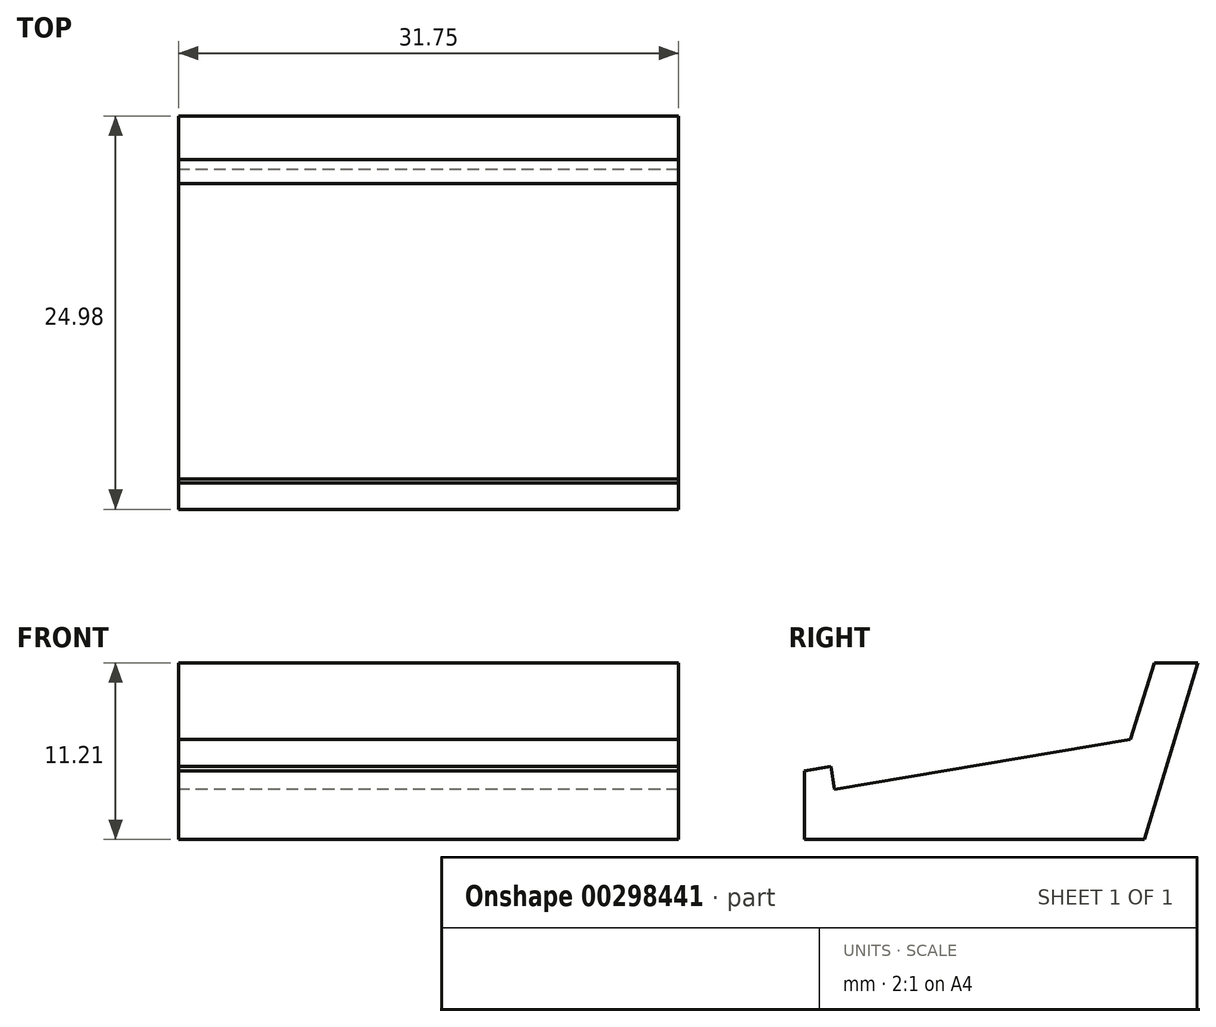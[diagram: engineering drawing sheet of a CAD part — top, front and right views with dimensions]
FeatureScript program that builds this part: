
annotation { "Feature Type Name" : "Feature", "Feature Type Description" : "" }
export const myFeature = defineFeature(function(context is Context, id is Id, definition is map)
    precondition{}
    {
        {
            var Q0;
            Q0=qCreatedBy(makeId("Right.planeOp"),FACE);
            var sketch = newSketch(context, id + "F0", { "sketchPlane" : qUnion([Q0])});
            skLineSegment(sketch, "E0", {"start": v(0, 0) * mm, "end": v(21.59, 0) * mm});
            skLineSegment(sketch, "E1", {"start": v(21.6, 0) * mm, "end": v(24.98, 11.21) * mm});
            skLineSegment(sketch, "E2", {"start": v(24.98, 11.21) * mm, "end": v(22.22, 11.21) * mm});
            skLineSegment(sketch, "E3", {"start": v(22.22, 11.21) * mm, "end": v(20.7, 6.35) * mm});
            skLineSegment(sketch, "E4", {"start": v(20.7, 6.35) * mm, "end": v(1.92, 3.17) * mm});
            skLineSegment(sketch, "E5", {"start": v(1.92, 3.17) * mm, "end": v(1.67, 4.62) * mm});
            skLineSegment(sketch, "E6", {"start": v(1.67, 4.62) * mm, "end": v(0, 4.34) * mm});
            skLineSegment(sketch, "E7", {"start": v(0, 4.34) * mm, "end": v(0, 0) * mm});
            skSolve(sketch);
        }
        {
            var Q0;
            Q0=makeQuery(id+"F0.imprint","IMPRINT",FACE,{"disambiguationData":[TD([[makeQuery(id+"F0.imprint","IMPRINT",EDGE,{"derivedFrom":sQuery(id+"F0.wireOp",EDGE,"E0")}),1.0]])]});
            extrude(context, id + "F1", {"entities" : qUnion([Q0]), "depth" : 31.75 * mm});
        }
    });
